# Revit family: Flexible Discharge Hose-JCI_Sapphire_Plus-(70bar)Novec1230
name_source: partatom
category: Specialty Equipment
revit_build: Autodesk Revit 2017 (Build: 20171027_0315(x64)
units: mm (PartAtom-declared; Revit-internal decimal feet)

## family parameters
Always vertical = Yes
Cut with Voids When Loaded = No
OmniClass Number = 23.29.33.13.11
Part Type = Normal
Room Calculation Point = No
Round Connector Dimension = Use Diameter
Shared = Yes
Work Plane-Based = Yes

## types (2) — shared parameters
A1 = 114 mm
Assembly Code = D4090300
Date Modified = YYYY/MM/DD
Default Elevation = 1219 mm
Description = Flexible Discharge Hose
Equipment Abbreviation = FH
Equipment Number = XXX
Family Version = 1.0
Fire Suppression Agent = 3M™ Novec™ 1230 Fire Protection Fluid
Manufacturer = Johnson Controls, Inc.
Model Disclaimer = For More Information Contact JOHNSON CONTROLS
Part Description = Flexible Discharge Hose
Product Documentation Link = http://www.sapphireplus.com
Product Page URL = http://www.sapphireplus.com
URL = http://www.sapphireplus.com
x = 65 mm  [stored 0.213255 ft]

## per-type parameters (varying)
| type | A | B | C | MR | Model | Part Number | b |
| 50mm | 144 mm | 520 mm  [stored 1.70604 ft] | 60 mm  [stored 0.19685 ft] | 30 mm  [stored 0.0984252 ft] | 306700002 | 306700002 | 70 mm  [stored 0.229659 ft] |
| 25mm | 82 mm | 405 mm | 30 mm  [stored 0.0984252 ft] | 16 mm  [stored 0.0524934 ft] | 306700001 | 306700001 | 42 mm  [stored 0.137795 ft] |

note: [stored X ft] marks values corroborated as IEEE doubles in the binary element streams (Revit-internal decimal feet)

## geometry (parser evidence)
native form markers: Sweep x2
no freeform markers — native parametric forms only
